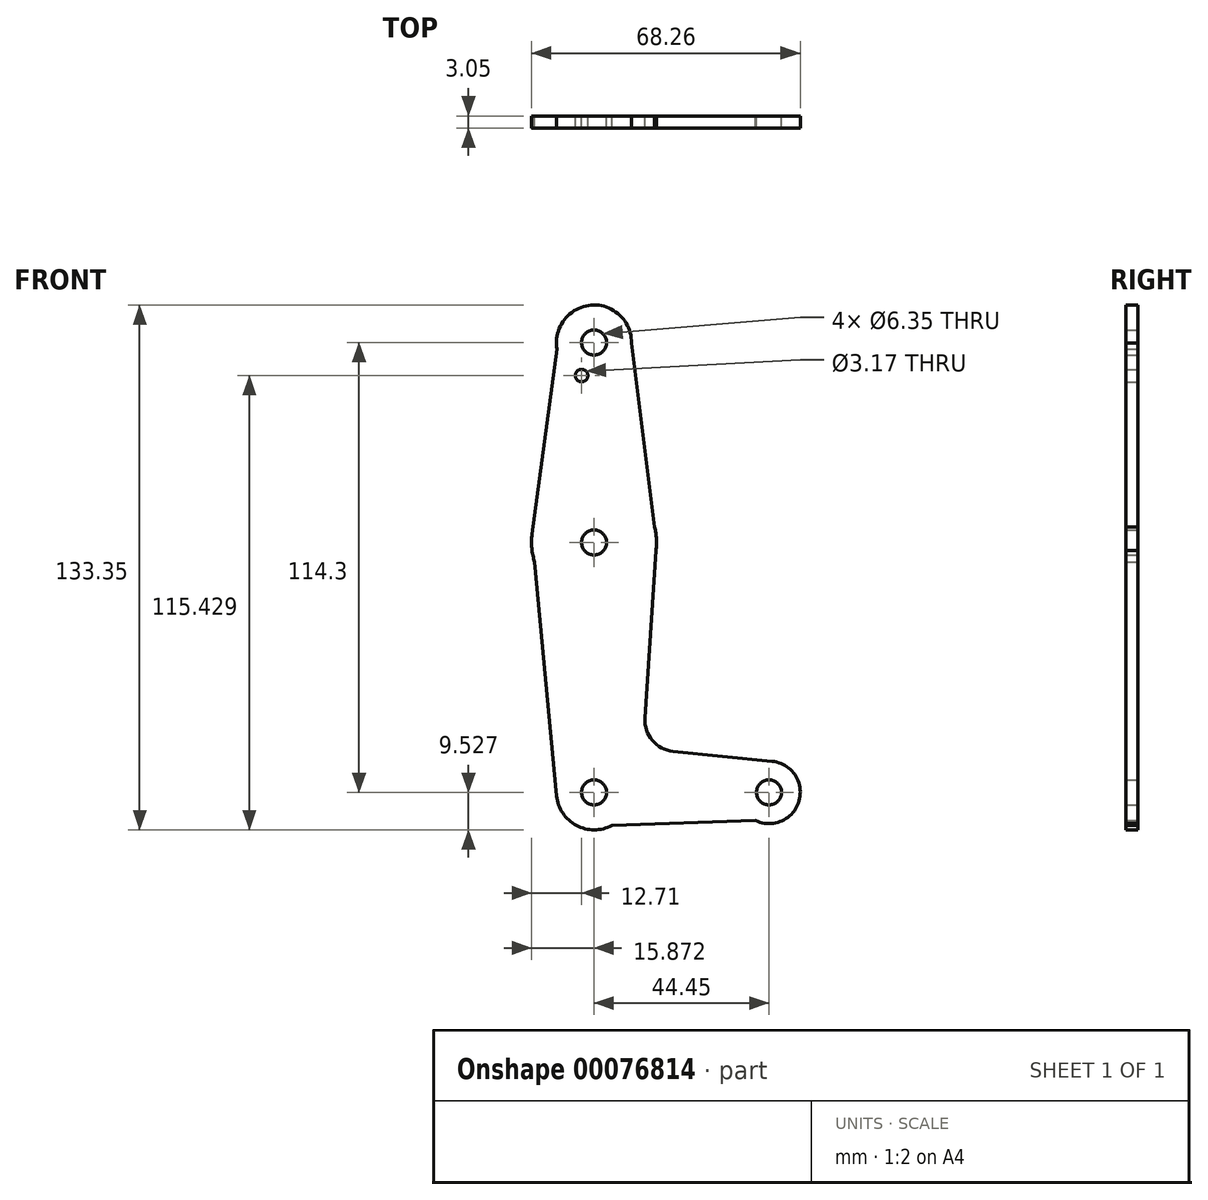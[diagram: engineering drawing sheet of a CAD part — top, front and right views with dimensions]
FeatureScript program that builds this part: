
annotation { "Feature Type Name" : "Feature", "Feature Type Description" : "" }
export const myFeature = defineFeature(function(context is Context, id is Id, definition is map)
    precondition{}
    {
        {
            var Q0;
            Q0=qCreatedBy(makeId("Front.planeOp"),FACE);
            var sketch = newSketch(context, id + "F0", { "sketchPlane" : qUnion([Q0])});
            skLineSegment(sketch, "E0", {"start": v(53.34, 51.2) * mm, "end": v(53.34, -63.1) * mm});
            skLineSegment(sketch, "E1", {"start": v(53.34, -63.1) * mm, "end": v(97.8, -63.1) * mm});
            skCircle(sketch, "E2", {"center": v(53.34, 51.2) * mm, "radius": 9.53 * mm});
            skCircle(sketch, "E3", {"center": v(53.34, 0.4) * mm, "radius": 15.88 * mm});
            skCircle(sketch, "E4", {"center": v(53.34, -63.1) * mm, "radius": 9.53 * mm});
            skCircle(sketch, "E5", {"center": v(97.8, -63.1) * mm, "radius": 7.94 * mm});
            skLineSegment(sketch, "E6", {"start": v(44.74, 55.28) * mm, "end": v(37.61, 2.52) * mm});
            skLineSegment(sketch, "E7", {"start": v(37.61, 2.52) * mm, "end": v(43.86, -64) * mm});
            skLineSegment(sketch, "E8", {"start": v(62.54, 53.69) * mm, "end": v(69.22, 0.4) * mm});
            skLineSegment(sketch, "E9", {"start": v(69.22, 0.4) * mm, "end": v(66.3, -44.23) * mm});
            skLineSegment(sketch, "E10", {"start": v(73.43, -52.66) * mm, "end": v(98.59, -55.2) * mm});
            skLineSegment(sketch, "E11", {"start": v(53.34, -63.1) * mm, "end": v(53.34, -72.63) * mm});
            skArc(sketch, "E12.filletArc", {"start": v(66.3, -44.23) * mm, "mid": v(68.16, -49.9) * mm, "end": v(73.43, -52.66) * mm});
            skCircle(sketch, "E13", {"center": v(53.34, 51.2) * mm, "radius": 3.18 * mm});
            skCircle(sketch, "E14", {"center": v(53.34, 0.4) * mm, "radius": 3.18 * mm});
            skCircle(sketch, "E15", {"center": v(53.34, -63.1) * mm, "radius": 3.18 * mm});
            skCircle(sketch, "E16", {"center": v(97.8, -63.1) * mm, "radius": 3.18 * mm});
            skCircle(sketch, "E17", {"center": v(50.18, 42.8) * mm, "radius": 1.59 * mm});
            skLineSegment(sketch, "E18", {"start": v(57.89, -71.47) * mm, "end": v(94.41, -70.28) * mm});
            skSolve(sketch);
        }
        {
            var Q0;
            Q0 = qSketchRegion(id + "F0", true);
            var Q1;
            {var subQ0=sQuery(id+"F0.wireOp",EDGE,"E4");var subQ1=sQuery(id+"F0.wireOp",EDGE,"E0");var subQ2=makeQuery(id+"F0.imprint","INTERSECT",VERTEX,{"derivedFrom":[subQ1,subQ0]});Q1=makeQuery(id+"F0.imprint","IMPRINT",FACE,{"disambiguationData":[TD([[makeQuery(id+"F0.imprint","IMPRINT",EDGE,{"disambiguationData":[TD([[subQ2,-1.0]])],"derivedFrom":subQ1}),1.0]])]});}
            extrude(context, id + "F1", {"entities" : qUnion([Q0, Q1]), "depth" : 3.05 * mm});
        }
    });
